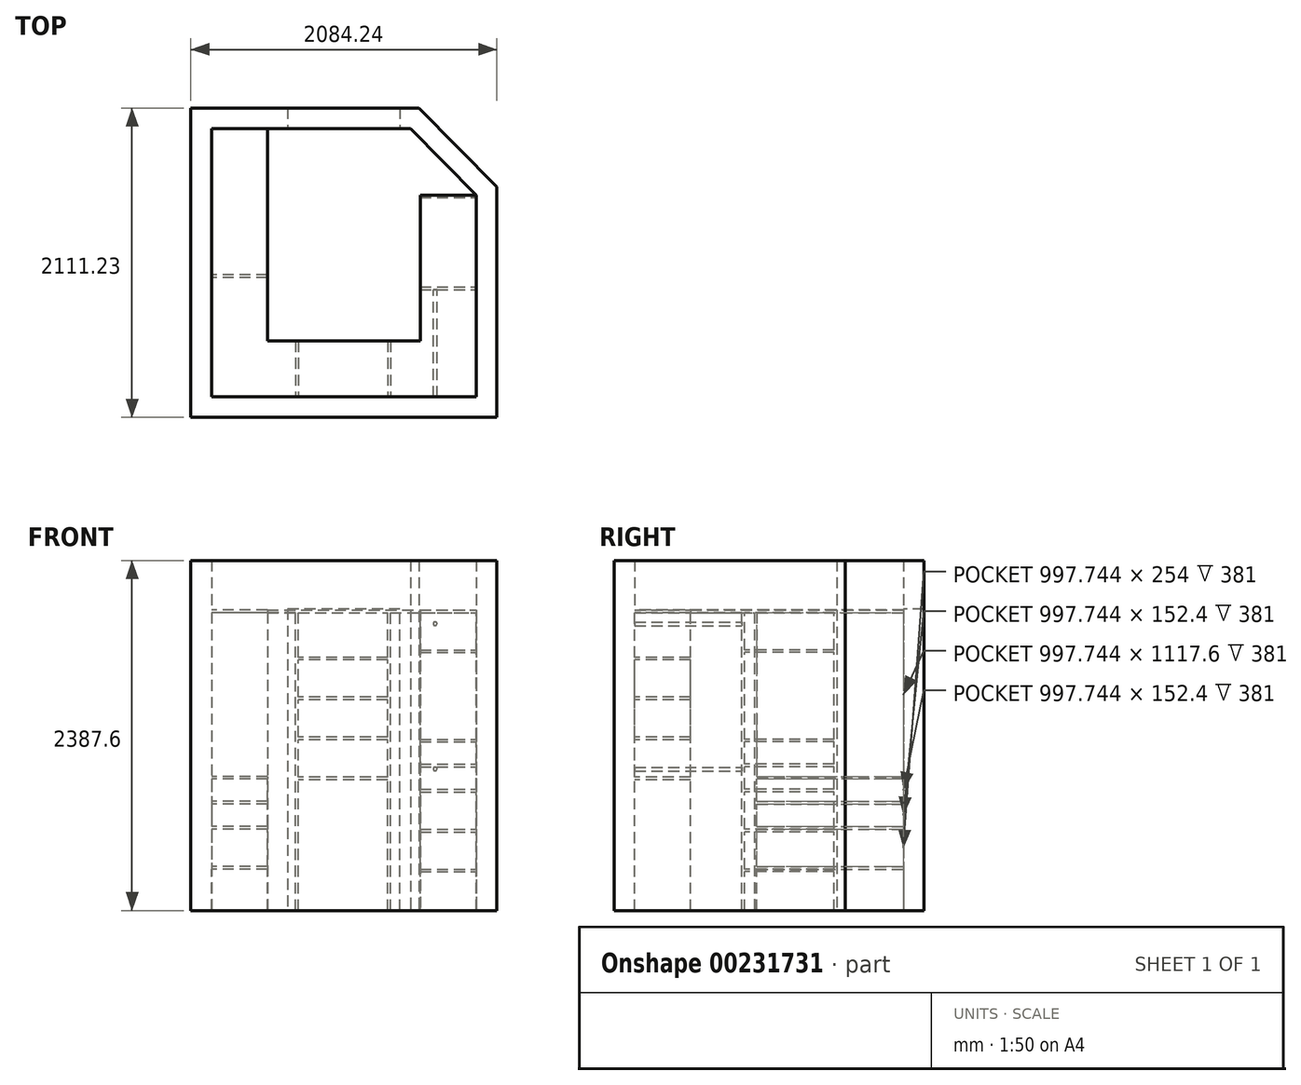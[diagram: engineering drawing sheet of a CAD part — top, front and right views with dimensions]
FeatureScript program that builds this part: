
annotation { "Feature Type Name" : "Feature", "Feature Type Description" : "" }
export const myFeature = defineFeature(function(context is Context, id is Id, definition is map)
    precondition{}
    {
        {
            var Q0;
            Q0=qCreatedBy(makeId("Top.planeOp"),FACE);
            var sketch = newSketch(context, id + "F0", { "sketchPlane" : qUnion([Q0])});
            skLineSegment(sketch, "E0", {"start": v(0, 0) * mm, "end": v(1803.4, 0) * mm});
            skLineSegment(sketch, "E1", {"start": v(0, 0) * mm, "end": v(0, 1830.39) * mm});
            skLineSegment(sketch, "E2", {"start": v(0, 1830.39) * mm, "end": v(1355.73, 1830.39) * mm});
            skLineSegment(sketch, "E3", {"start": v(1803.4, 0) * mm, "end": v(1803.4, 1376.36) * mm});
            skLineSegment(sketch, "E4", {"start": v(1355.73, 1830.39) * mm, "end": v(1803.4, 1376.36) * mm});
            skLineSegment(sketch, "E5.0", {"start": v(-132.08, 1962.47) * mm, "end": v(1355.73, 1962.47) * mm});
            skLineSegment(sketch, "E5.1", {"start": v(-132.08, 0) * mm, "end": v(-132.08, 1962.47) * mm});
            skLineSegment(sketch, "E6.0", {"start": v(0, -6.35) * mm, "end": v(1803.4, -6.35) * mm});
            skLineSegment(sketch, "E7.0", {"start": v(1943.82, -140.42) * mm, "end": v(1943.82, 1433.95) * mm});
            skLineSegment(sketch, "E7.1", {"start": v(-140.42, -140.42) * mm, "end": v(1943.82, -140.42) * mm});
            skLineSegment(sketch, "E7.2", {"start": v(1414.47, 1970.81) * mm, "end": v(1943.82, 1433.95) * mm});
            skLineSegment(sketch, "E7.3", {"start": v(-140.42, 1970.81) * mm, "end": v(1414.47, 1970.81) * mm});
            skLineSegment(sketch, "E7.4", {"start": v(-140.42, -140.42) * mm, "end": v(-140.42, 1970.81) * mm});
            skSolve(sketch);
        }
        {
            var Q0;
            Q0=makeQuery(id+"F0.imprint","IMPRINT",FACE,{"disambiguationData":[TD([[makeQuery(id+"F0.imprint","IMPRINT",EDGE,{"derivedFrom":sQuery(id+"F0.wireOp",EDGE,"E0")}),-1.0]])]});
            extrude(context, id + "F1", {"entities" : qUnion([Q0]), "depth" : 2387.6 * mm});
        }
        {
            var Q0;
            Q0=makeQuery(id+"F1.opExtrude","SWEPT_FACE",FACE,{"disambiguationData":[OSD([sQuery(id+"F0.wireOp",EDGE,"E2")])]});
            var sketch = newSketch(context, id + "F2", { "sketchPlane" : qUnion([Q0])});
            skLineSegment(sketch, "E8", {"start": v(1284.29, 0) * mm, "end": v(1284.29, 2057.4) * mm});
            skLineSegment(sketch, "E9", {"start": v(1284.29, 2057.4) * mm, "end": v(517.52, 2057.4) * mm});
            skLineSegment(sketch, "E10", {"start": v(517.52, 2057.4) * mm, "end": v(517.52, 0) * mm});
            skLineSegment(sketch, "E11", {"start": v(1284.29, 0) * mm, "end": v(517.52, 0) * mm});
            skSolve(sketch);
        }
        {
            var Q0;
            Q0=makeQuery(id+"F2.imprint","IMPRINT",FACE,{"disambiguationData":[TD([[makeQuery(id+"F2.imprint","IMPRINT",EDGE,{"derivedFrom":sQuery(id+"F2.wireOp",EDGE,"E8")}),1.0]])]});
            extrude(context, id + "F3", {"entities" : qUnion([Q0]), "operationType" : NewBodyOperationType.REMOVE, "endBound" : BoundingType.THROUGH_ALL, "oppositeDirection" : true, "depth" : 25.4 * mm});
        }
        {
            var Q0;
            Q0=makeQuery(id+"F1.opExtrude","SWEPT_FACE",FACE,{"disambiguationData":[OSD([sQuery(id+"F0.wireOp",EDGE,"E1")])]});
            var sketch = newSketch(context, id + "F4", { "sketchPlane" : qUnion([Q0])});
            skLineSegment(sketch, "E12", {"start": v(814.39, 914.4) * mm, "end": v(1830.39, 914.4) * mm});
            skLineSegment(sketch, "E13.0", {"start": v(0, 0) * mm, "end": v(1830.39, 0) * mm});
            skLineSegment(sketch, "E13.1", {"start": v(0, 2387.6) * mm, "end": v(0, 0) * mm});
            skLineSegment(sketch, "E13.2", {"start": v(1830.39, 2387.6) * mm, "end": v(0, 2387.6) * mm});
            skLineSegment(sketch, "E13.3", {"start": v(1830.39, 0) * mm, "end": v(1830.39, 2387.6) * mm});
            skLineSegment(sketch, "E14", {"start": v(814.39, 0) * mm, "end": v(832.64, 0) * mm});
            skLineSegment(sketch, "E15", {"start": v(814.39, 914.4) * mm, "end": v(814.39, 0) * mm});
            skLineSegment(sketch, "E16", {"start": v(1830.39, 914.4) * mm, "end": v(1830.39, 896.14) * mm});
            skLineSegment(sketch, "E17", {"start": v(832.64, 0) * mm, "end": v(832.64, 896.14) * mm});
            skLineSegment(sketch, "E18", {"start": v(1830.39, 896.14) * mm, "end": v(832.64, 896.14) * mm});
            skSolve(sketch);
        }
        {
            var Q0;
            Q0=makeQuery(id+"F4.imprint","IMPRINT",FACE,{"disambiguationData":[TD([[makeQuery(id+"F4.imprint","IMPRINT",EDGE,{"derivedFrom":sQuery(id+"F4.wireOp",EDGE,"E12")}),-1.0]])]});
            extrude(context, id + "F5", {"entities" : qUnion([Q0]), "operationType" : NewBodyOperationType.ADD, "depth" : 381 * mm});
        }
        {
            var Q0;
            {var subQ8=sQuery(id+"F0.wireOp",EDGE,"E1");var subQ9=sQuery(id+"F0.wireOp",EDGE,"E0");Q0=makeQuery(id+"F5.boolean.opBoolean","SPLIT",FACE,{"disambiguationData":[TD([makeQuery(id+"F1.opExtrude","SWEPT_FACE",FACE,{"disambiguationData":[OSD([subQ9])]})])],"derivedFrom":makeQuery(id+"F1.opExtrude","SWEPT_FACE",FACE,{"disambiguationData":[OSD([subQ8])]})});}
            var sketch = newSketch(context, id + "F6", { "sketchPlane" : qUnion([Q0])});
            skLineSegment(sketch, "E19", {"start": v(814.39, 914.4) * mm, "end": v(814.39, 2032) * mm});
            skLineSegment(sketch, "E20", {"start": v(814.39, 2032) * mm, "end": v(832.64, 2032) * mm});
            skLineSegment(sketch, "E21", {"start": v(832.64, 2032) * mm, "end": v(832.64, 914.4) * mm});
            skLineSegment(sketch, "E22", {"start": v(832.64, 914.4) * mm, "end": v(814.39, 914.4) * mm});
            skSolve(sketch);
        }
        {
            var Q0;
            Q0 = qSketchRegion(id + "F6", true);
            extrude(context, id + "F7", {"entities" : qUnion([Q0]), "operationType" : NewBodyOperationType.ADD, "depth" : 381 * mm});
        }
        {
            var Q0;
            {var subQ8=sQuery(id+"F0.wireOp",EDGE,"E1");var subQ9=sQuery(id+"F0.wireOp",EDGE,"E0");Q0=makeQuery(id+"F5.boolean.opBoolean","SPLIT",FACE,{"disambiguationData":[TD([makeQuery(id+"F1.opExtrude","SWEPT_FACE",FACE,{"disambiguationData":[OSD([subQ9])]})])],"derivedFrom":makeQuery(id+"F1.opExtrude","SWEPT_FACE",FACE,{"disambiguationData":[OSD([subQ8])]})});}
            var sketch = newSketch(context, id + "F8", { "sketchPlane" : qUnion([Q0])});
            skLineSegment(sketch, "E23", {"start": v(832.64, 2032) * mm, "end": v(1830.39, 2032) * mm});
            skLineSegment(sketch, "E24", {"start": v(1830.39, 2032) * mm, "end": v(1830.39, 2050.26) * mm});
            skLineSegment(sketch, "E25", {"start": v(1830.39, 2050.26) * mm, "end": v(0, 2050.26) * mm});
            skLineSegment(sketch, "E26", {"start": v(0, 2050.26) * mm, "end": v(0, 2032) * mm});
            skLineSegment(sketch, "E27", {"start": v(0, 2032) * mm, "end": v(814.39, 2032) * mm});
            skLineSegment(sketch, "E28", {"start": v(814.39, 2032) * mm, "end": v(832.64, 2032) * mm});
            skSolve(sketch);
        }
        {
            var Q0;
            Q0 = qSketchRegion(id + "F8", true);
            extrude(context, id + "F9", {"entities" : qUnion([Q0]), "operationType" : NewBodyOperationType.ADD, "depth" : 381 * mm});
        }
        {
            var Q0;
            {var subQ1=sQuery(id+"F0.wireOp",EDGE,"E1");Q0=makeQuery(id+"F5.boolean.opBoolean","SPLIT",FACE,{"disambiguationData":[TD([makeQuery(id+"F5.opExtrude","SWEPT_FACE",FACE,{"disambiguationData":[OSD([sQuery(id+"F4.wireOp",EDGE,"E17")])]})])],"derivedFrom":makeQuery(id+"F1.opExtrude","SWEPT_FACE",FACE,{"disambiguationData":[OSD([subQ1])]})});}
            var sketch = newSketch(context, id + "F10", { "sketchPlane" : qUnion([Q0])});
            skLineSegment(sketch, "E29.bottom", {"start": v(832.64, 743.74) * mm, "end": v(1830.39, 743.74) * mm});
            skLineSegment(sketch, "E29.top", {"start": v(832.64, 725.49) * mm, "end": v(1830.39, 725.49) * mm});
            skLineSegment(sketch, "E29.left", {"start": v(832.64, 743.74) * mm, "end": v(832.64, 725.49) * mm});
            skLineSegment(sketch, "E29.right", {"start": v(1830.39, 743.74) * mm, "end": v(1830.39, 725.49) * mm});
            skLineSegment(sketch, "E30.bottom", {"start": v(832.64, 573.09) * mm, "end": v(1830.39, 573.09) * mm});
            skLineSegment(sketch, "E30.top", {"start": v(832.64, 554.82) * mm, "end": v(1830.39, 554.82) * mm});
            skLineSegment(sketch, "E30.left", {"start": v(832.64, 573.09) * mm, "end": v(832.64, 554.82) * mm});
            skLineSegment(sketch, "E30.right", {"start": v(1830.39, 573.09) * mm, "end": v(1830.39, 554.82) * mm});
            skLineSegment(sketch, "E31.bottom", {"start": v(832.64, 300.82) * mm, "end": v(1830.39, 300.82) * mm});
            skLineSegment(sketch, "E31.top", {"start": v(832.64, 282.56) * mm, "end": v(1830.39, 282.56) * mm});
            skLineSegment(sketch, "E31.left", {"start": v(832.64, 300.82) * mm, "end": v(832.64, 282.56) * mm});
            skLineSegment(sketch, "E31.right", {"start": v(1830.39, 300.82) * mm, "end": v(1830.39, 282.56) * mm});
            skSolve(sketch);
        }
        {
            var Q0;
            Q0 = qSketchRegion(id + "F10", true);
            extrude(context, id + "F11", {"entities" : qUnion([Q0]), "operationType" : NewBodyOperationType.ADD, "depth" : 381 * mm});
        }
        {
            var Q0;
            Q0=makeQuery(id+"F7.opExtrude","SWEPT_FACE",FACE,{"disambiguationData":[OSD([sQuery(id+"F6.wireOp",EDGE,"E21")])]});
            var sketch = newSketch(context, id + "F12", { "sketchPlane" : qUnion([Q0])});
            skCircle(sketch, "E32", {"center": v(-279.4, 1955.8) * mm, "radius": 12.7 * mm});
            skSolve(sketch);
        }
        {
            var Q0;
            Q0=sQuery(id+"F12.wireOp",EDGE,"E32");
            extrude(context, id + "F13", {"bodyType" : ToolBodyType.SURFACE, "surfaceEntities" : qUnion([Q0]), "endBound" : BoundingType.UP_TO_NEXT, "depth" : 25.4 * mm});
        }
        {
            var Q0;
            Q0=makeQuery(id+"F7.boolean.opBoolean","MERGE",FACE,{"derivedFrom":[makeQuery(id+"F5.opExtrude","SWEPT_FACE",FACE,{"disambiguationData":[OSD([sQuery(id+"F4.wireOp",EDGE,"E15")])]}),makeQuery(id+"F7.opExtrude","SWEPT_FACE",FACE,{"disambiguationData":[OSD([sQuery(id+"F6.wireOp",EDGE,"E19")])]})]});
            var sketch = newSketch(context, id + "F14", { "sketchPlane" : qUnion([Q0])});
            skCircle(sketch, "E33", {"center": v(279.4, 1955.8) * mm, "radius": 12.7 * mm});
            skSolve(sketch);
        }
        {
            var Q0;
            Q0=sQuery(id+"F14.wireOp",EDGE,"E33");
            extrude(context, id + "F15", {"bodyType" : ToolBodyType.SURFACE, "surfaceEntities" : qUnion([Q0]), "endBound" : BoundingType.UP_TO_NEXT, "depth" : 25.4 * mm});
        }
        {
            var Q0;
            Q0=makeQuery(id+"F1.opExtrude","SWEPT_FACE",FACE,{"disambiguationData":[OSD([sQuery(id+"F0.wireOp",EDGE,"E3")])]});
            var sketch = newSketch(context, id + "F16", { "sketchPlane" : qUnion([Q0])});
            skLineSegment(sketch, "E34.bottom", {"start": v(-1376.36, 0) * mm, "end": v(-1358.1, 0) * mm});
            skLineSegment(sketch, "E34.top", {"start": v(-1376.36, 2032) * mm, "end": v(-1358.1, 2032) * mm});
            skLineSegment(sketch, "E34.left", {"start": v(-1376.36, 0) * mm, "end": v(-1376.36, 2032) * mm});
            skLineSegment(sketch, "E34.right", {"start": v(-1358.1, 0) * mm, "end": v(-1358.1, 2032) * mm});
            skLineSegment(sketch, "E35.bottom", {"start": v(-748.5, 0) * mm, "end": v(-730.24, 0) * mm});
            skLineSegment(sketch, "E35.top", {"start": v(-748.5, 2032) * mm, "end": v(-730.24, 2032) * mm});
            skLineSegment(sketch, "E35.left", {"start": v(-748.5, 0) * mm, "end": v(-748.5, 2032) * mm});
            skLineSegment(sketch, "E35.right", {"start": v(-730.24, 0) * mm, "end": v(-730.24, 2032) * mm});
            skSolve(sketch);
        }
        {
            var Q0;
            Q0 = qSketchRegion(id + "F16", true);
            extrude(context, id + "F17", {"entities" : qUnion([Q0]), "operationType" : NewBodyOperationType.ADD, "depth" : 381 * mm});
        }
        {
            var Q0;
            Q0=makeQuery(id+"F1.opExtrude","SWEPT_FACE",FACE,{"disambiguationData":[OSD([sQuery(id+"F0.wireOp",EDGE,"E3")])]});
            var sketch = newSketch(context, id + "F18", { "sketchPlane" : qUnion([Q0])});
            skLineSegment(sketch, "E36.bottom", {"start": v(-1376.36, 2032) * mm, "end": v(0, 2032) * mm});
            skLineSegment(sketch, "E36.top", {"start": v(-1376.36, 2050.26) * mm, "end": v(0, 2050.26) * mm});
            skLineSegment(sketch, "E36.left", {"start": v(-1376.36, 2032) * mm, "end": v(-1376.36, 2050.26) * mm});
            skLineSegment(sketch, "E36.right", {"start": v(0, 2032) * mm, "end": v(0, 2050.26) * mm});
            skSolve(sketch);
        }
        {
            var Q0;
            Q0=makeQuery(id+"F18.imprint","IMPRINT",FACE,{"disambiguationData":[TD([[makeQuery(id+"F18.imprint","IMPRINT",EDGE,{"derivedFrom":sQuery(id+"F18.wireOp",EDGE,"E36.top")}),-1.0]])]});
            extrude(context, id + "F19", {"entities" : qUnion([Q0]), "operationType" : NewBodyOperationType.ADD, "depth" : 381 * mm});
        }
        {
            var Q0;
            Q0=makeQuery(id+"F17.opExtrude","SWEPT_FACE",FACE,{"disambiguationData":[OSD([sQuery(id+"F16.wireOp",EDGE,"E35.right")])]});
            var sketch = newSketch(context, id + "F20", { "sketchPlane" : qUnion([Q0])});
            skCircle(sketch, "E37", {"center": v(1524, 1955.8) * mm, "radius": 12.7 * mm});
            skCircle(sketch, "E38", {"center": v(1524, 965.2) * mm, "radius": 12.7 * mm});
            skSolve(sketch);
        }
        {
            var Q0;
            Q0=makeQuery(id+"F20.imprint","IMPRINT",FACE,{"disambiguationData":[TD([[makeQuery(id+"F20.imprint","IMPRINT",EDGE,{"derivedFrom":sQuery(id+"F20.wireOp",EDGE,"E37")}),1.0]])]});
            extrude(context, id + "F21", {"entities" : qUnion([Q0]), "operationType" : NewBodyOperationType.ADD, "endBound" : BoundingType.UP_TO_NEXT, "depth" : 25.4 * mm});
        }
        {
            var Q0;
            Q0 = qSketchRegion(id + "F20", true);
            extrude(context, id + "F22", {"entities" : qUnion([Q0]), "operationType" : NewBodyOperationType.ADD, "endBound" : BoundingType.UP_TO_NEXT, "depth" : 25.4 * mm});
        }
        {
            var Q0;
            {var subQ0=sQuery(id+"F0.wireOp",EDGE,"E3");Q0=makeQuery(id+"F19.boolean.opBoolean","SPLIT",FACE,{"disambiguationData":[TD([makeQuery(id+"F17.opExtrude","SWEPT_FACE",FACE,{"disambiguationData":[OSD([sQuery(id+"F16.wireOp",EDGE,"E34.right")])]})])],"derivedFrom":makeQuery(id+"F1.opExtrude","SWEPT_FACE",FACE,{"disambiguationData":[OSD([subQ0])]})});}
            var sketch = newSketch(context, id + "F23", { "sketchPlane" : qUnion([Q0])});
            skLineSegment(sketch, "E39.bottom", {"start": v(-1358.1, 1759.74) * mm, "end": v(-748.5, 1759.74) * mm});
            skLineSegment(sketch, "E39.top", {"start": v(-1358.1, 1778) * mm, "end": v(-748.5, 1778) * mm});
            skLineSegment(sketch, "E39.left", {"start": v(-1358.1, 1759.74) * mm, "end": v(-1358.1, 1778) * mm});
            skLineSegment(sketch, "E39.right", {"start": v(-748.5, 1759.74) * mm, "end": v(-748.5, 1778) * mm});
            skLineSegment(sketch, "E40.bottom", {"start": v(-1358.1, 1168.4) * mm, "end": v(-748.5, 1168.4) * mm});
            skLineSegment(sketch, "E40.top", {"start": v(-1358.1, 1150.14) * mm, "end": v(-748.5, 1150.14) * mm});
            skLineSegment(sketch, "E40.left", {"start": v(-1358.1, 1168.4) * mm, "end": v(-1358.1, 1150.14) * mm});
            skLineSegment(sketch, "E40.right", {"start": v(-748.5, 1168.4) * mm, "end": v(-748.5, 1150.14) * mm});
            skLineSegment(sketch, "E41.bottom", {"start": v(-1358.1, 997.74) * mm, "end": v(-748.5, 997.74) * mm});
            skLineSegment(sketch, "E41.top", {"start": v(-1358.1, 979.47) * mm, "end": v(-748.5, 979.47) * mm});
            skLineSegment(sketch, "E41.left", {"start": v(-1358.1, 997.74) * mm, "end": v(-1358.1, 979.47) * mm});
            skLineSegment(sketch, "E41.right", {"start": v(-748.5, 997.74) * mm, "end": v(-748.5, 979.47) * mm});
            skLineSegment(sketch, "E42.bottom", {"start": v(-1358.1, 827.07) * mm, "end": v(-748.5, 827.07) * mm});
            skLineSegment(sketch, "E42.top", {"start": v(-1358.1, 808.81) * mm, "end": v(-748.5, 808.81) * mm});
            skLineSegment(sketch, "E42.left", {"start": v(-1358.1, 827.07) * mm, "end": v(-1358.1, 808.81) * mm});
            skLineSegment(sketch, "E42.right", {"start": v(-748.5, 827.07) * mm, "end": v(-748.5, 808.81) * mm});
            skLineSegment(sketch, "E43.bottom", {"start": v(-1358.1, 554.81) * mm, "end": v(-748.5, 554.81) * mm});
            skLineSegment(sketch, "E43.top", {"start": v(-1358.1, 536.55) * mm, "end": v(-748.5, 536.55) * mm});
            skLineSegment(sketch, "E43.left", {"start": v(-1358.1, 554.81) * mm, "end": v(-1358.1, 536.55) * mm});
            skLineSegment(sketch, "E43.right", {"start": v(-748.5, 554.81) * mm, "end": v(-748.5, 536.55) * mm});
            skLineSegment(sketch, "E44.bottom", {"start": v(-1358.1, 282.55) * mm, "end": v(-748.5, 282.55) * mm});
            skLineSegment(sketch, "E44.top", {"start": v(-1358.1, 264.29) * mm, "end": v(-748.5, 264.29) * mm});
            skLineSegment(sketch, "E44.left", {"start": v(-1358.1, 282.55) * mm, "end": v(-1358.1, 264.29) * mm});
            skLineSegment(sketch, "E44.right", {"start": v(-748.5, 282.55) * mm, "end": v(-748.5, 264.29) * mm});
            skSolve(sketch);
        }
        {
            var Q0;
            Q0 = qSketchRegion(id + "F23", true);
            extrude(context, id + "F24", {"entities" : qUnion([Q0]), "operationType" : NewBodyOperationType.ADD, "depth" : 381 * mm});
        }
        {
            var Q0;
            Q0=makeQuery(id+"F1.opExtrude","SWEPT_FACE",FACE,{"disambiguationData":[OSD([sQuery(id+"F0.wireOp",EDGE,"E0")])]});
            var sketch = newSketch(context, id + "F25", { "sketchPlane" : qUnion([Q0])});
            skLineSegment(sketch, "E45.bottom", {"start": v(-1219.2, 0) * mm, "end": v(-1200.94, 0) * mm});
            skLineSegment(sketch, "E45.top", {"start": v(-1219.2, 2032) * mm, "end": v(-1200.94, 2032) * mm});
            skLineSegment(sketch, "E45.left", {"start": v(-1219.2, 0) * mm, "end": v(-1219.2, 2032) * mm});
            skLineSegment(sketch, "E45.right", {"start": v(-1200.94, 0) * mm, "end": v(-1200.94, 2032) * mm});
            skLineSegment(sketch, "E46.bottom", {"start": v(-591.34, 0) * mm, "end": v(-573.07, 0) * mm});
            skLineSegment(sketch, "E46.top", {"start": v(-591.34, 2032) * mm, "end": v(-573.07, 2032) * mm});
            skLineSegment(sketch, "E46.left", {"start": v(-591.34, 0) * mm, "end": v(-591.34, 2032) * mm});
            skLineSegment(sketch, "E46.right", {"start": v(-573.07, 0) * mm, "end": v(-573.07, 2032) * mm});
            skSolve(sketch);
        }
        {
            var Q0;
            Q0 = qSketchRegion(id + "F25", true);
            extrude(context, id + "F26", {"entities" : qUnion([Q0]), "operationType" : NewBodyOperationType.ADD, "depth" : 381 * mm});
        }
        {
            var Q0;
            Q0=makeQuery(id+"F1.opExtrude","SWEPT_FACE",FACE,{"disambiguationData":[OSD([sQuery(id+"F0.wireOp",EDGE,"E0")])]});
            var sketch = newSketch(context, id + "F27", { "sketchPlane" : qUnion([Q0])});
            skLineSegment(sketch, "E47.bottom", {"start": v(-381, 2032) * mm, "end": v(-1422.4, 2032) * mm});
            skLineSegment(sketch, "E47.top", {"start": v(-381, 2050.26) * mm, "end": v(-1422.4, 2050.26) * mm});
            skLineSegment(sketch, "E47.left", {"start": v(-381, 2032) * mm, "end": v(-381, 2050.26) * mm});
            skLineSegment(sketch, "E47.right", {"start": v(-1422.4, 2032) * mm, "end": v(-1422.4, 2050.26) * mm});
            skSolve(sketch);
        }
        {
            var Q0;
            Q0 = qSketchRegion(id + "F27", true);
            extrude(context, id + "F28", {"entities" : qUnion([Q0]), "operationType" : NewBodyOperationType.ADD, "depth" : 381 * mm});
        }
        {
            var Q0;
            {var subQ0=sQuery(id+"F0.wireOp",EDGE,"E0");Q0=makeQuery(id+"F28.boolean.opBoolean","SPLIT",FACE,{"disambiguationData":[TD([makeQuery(id+"F26.opExtrude","SWEPT_FACE",FACE,{"disambiguationData":[OSD([sQuery(id+"F25.wireOp",EDGE,"E45.right")])]})])],"derivedFrom":makeQuery(id+"F1.opExtrude","SWEPT_FACE",FACE,{"disambiguationData":[OSD([subQ0])]})});}
            var sketch = newSketch(context, id + "F29", { "sketchPlane" : qUnion([Q0])});
            skLineSegment(sketch, "E48.bottom", {"start": v(-1200.94, 1727.2) * mm, "end": v(-591.34, 1727.2) * mm});
            skLineSegment(sketch, "E48.top", {"start": v(-1200.94, 1708.94) * mm, "end": v(-591.34, 1708.94) * mm});
            skLineSegment(sketch, "E48.left", {"start": v(-1200.94, 1727.2) * mm, "end": v(-1200.94, 1708.94) * mm});
            skLineSegment(sketch, "E48.right", {"start": v(-591.34, 1727.2) * mm, "end": v(-591.34, 1708.94) * mm});
            skLineSegment(sketch, "E49.bottom", {"start": v(-1200.94, 1454.94) * mm, "end": v(-591.34, 1454.94) * mm});
            skLineSegment(sketch, "E49.top", {"start": v(-1200.94, 1436.67) * mm, "end": v(-591.34, 1436.67) * mm});
            skLineSegment(sketch, "E49.left", {"start": v(-1200.94, 1454.94) * mm, "end": v(-1200.94, 1436.67) * mm});
            skLineSegment(sketch, "E49.right", {"start": v(-591.34, 1454.94) * mm, "end": v(-591.34, 1436.67) * mm});
            skLineSegment(sketch, "E50.bottom", {"start": v(-1200.94, 1182.67) * mm, "end": v(-591.34, 1182.67) * mm});
            skLineSegment(sketch, "E50.top", {"start": v(-1200.94, 1164.41) * mm, "end": v(-591.34, 1164.41) * mm});
            skLineSegment(sketch, "E50.left", {"start": v(-1200.94, 1182.67) * mm, "end": v(-1200.94, 1164.41) * mm});
            skLineSegment(sketch, "E50.right", {"start": v(-591.34, 1182.67) * mm, "end": v(-591.34, 1164.41) * mm});
            skLineSegment(sketch, "E51.bottom", {"start": v(-1200.94, 910.41) * mm, "end": v(-591.34, 910.41) * mm});
            skLineSegment(sketch, "E51.top", {"start": v(-1200.94, 892.15) * mm, "end": v(-591.34, 892.15) * mm});
            skLineSegment(sketch, "E51.left", {"start": v(-1200.94, 910.41) * mm, "end": v(-1200.94, 892.15) * mm});
            skLineSegment(sketch, "E51.right", {"start": v(-591.34, 910.41) * mm, "end": v(-591.34, 892.15) * mm});
            skSolve(sketch);
        }
        {
            var Q0;
            Q0 = qSketchRegion(id + "F29", true);
            extrude(context, id + "F30", {"entities" : qUnion([Q0]), "operationType" : NewBodyOperationType.ADD, "depth" : 381 * mm});
        }
    });
